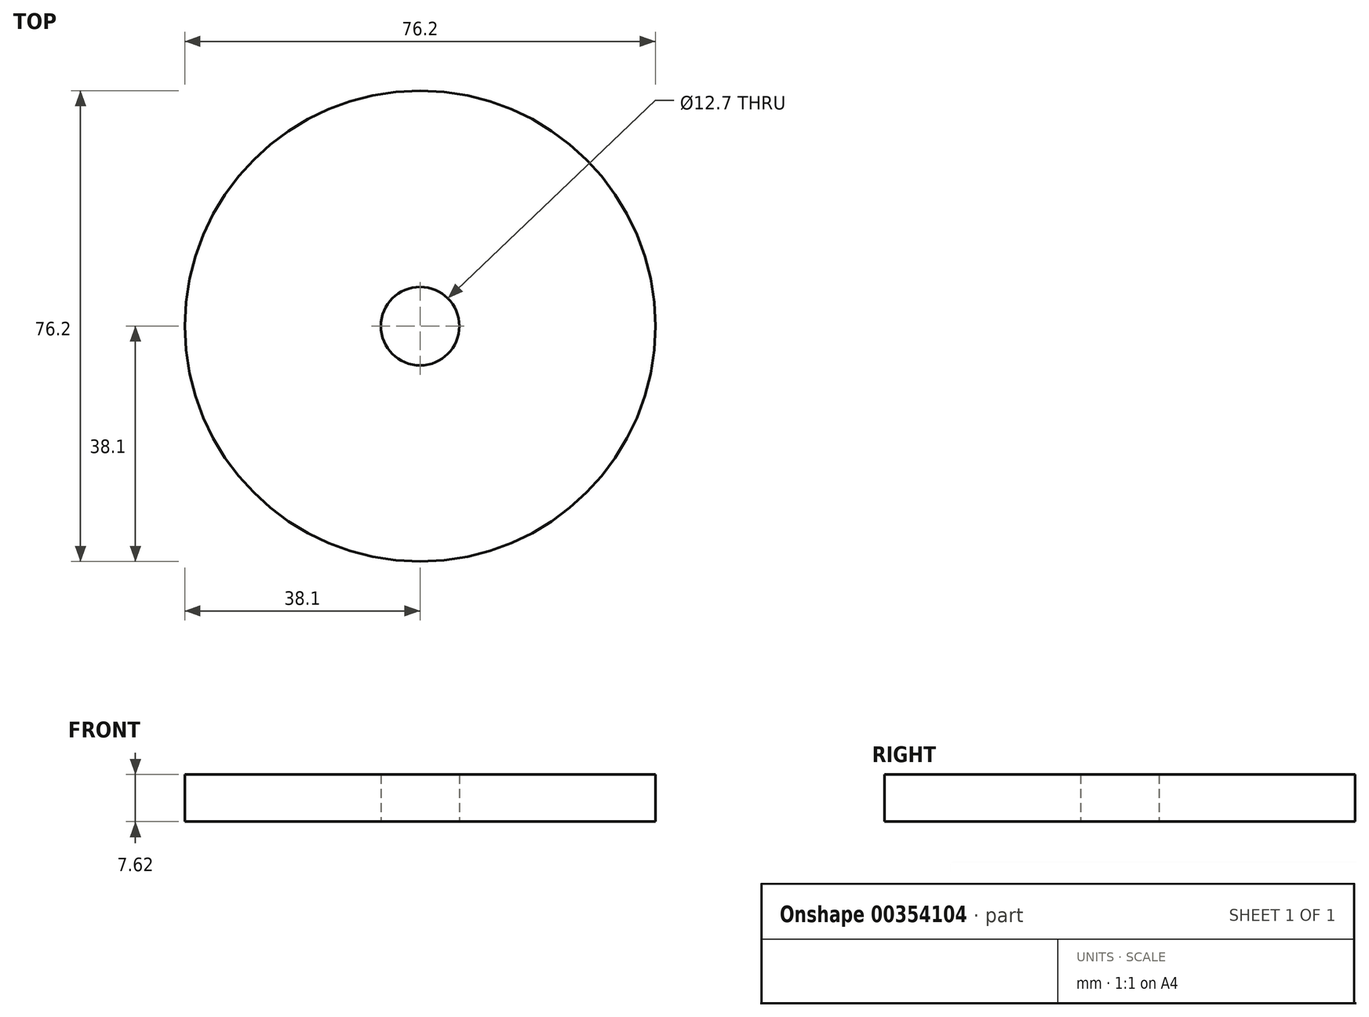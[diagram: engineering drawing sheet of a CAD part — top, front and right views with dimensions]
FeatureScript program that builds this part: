
annotation { "Feature Type Name" : "Feature", "Feature Type Description" : "" }
export const myFeature = defineFeature(function(context is Context, id is Id, definition is map)
    precondition{}
    {
        {
            var Q0;
            Q0=qCreatedBy(makeId("Top.planeOp"),FACE);
            var sketch = newSketch(context, id + "F0", { "sketchPlane" : qUnion([Q0])});
            skCircle(sketch, "E0", {"center": v(0, 0) * mm, "radius": 38.1 * mm});
            skCircle(sketch, "E1", {"center": v(0, 0) * mm, "radius": 6.35 * mm});
            skSolve(sketch);
        }
        {
            var Q0;
            Q0 = qSketchRegion(id + "F0", true);
            extrude(context, id + "F1", {"entities" : qUnion([Q0]), "depth" : 7.62 * mm});
        }
    });
